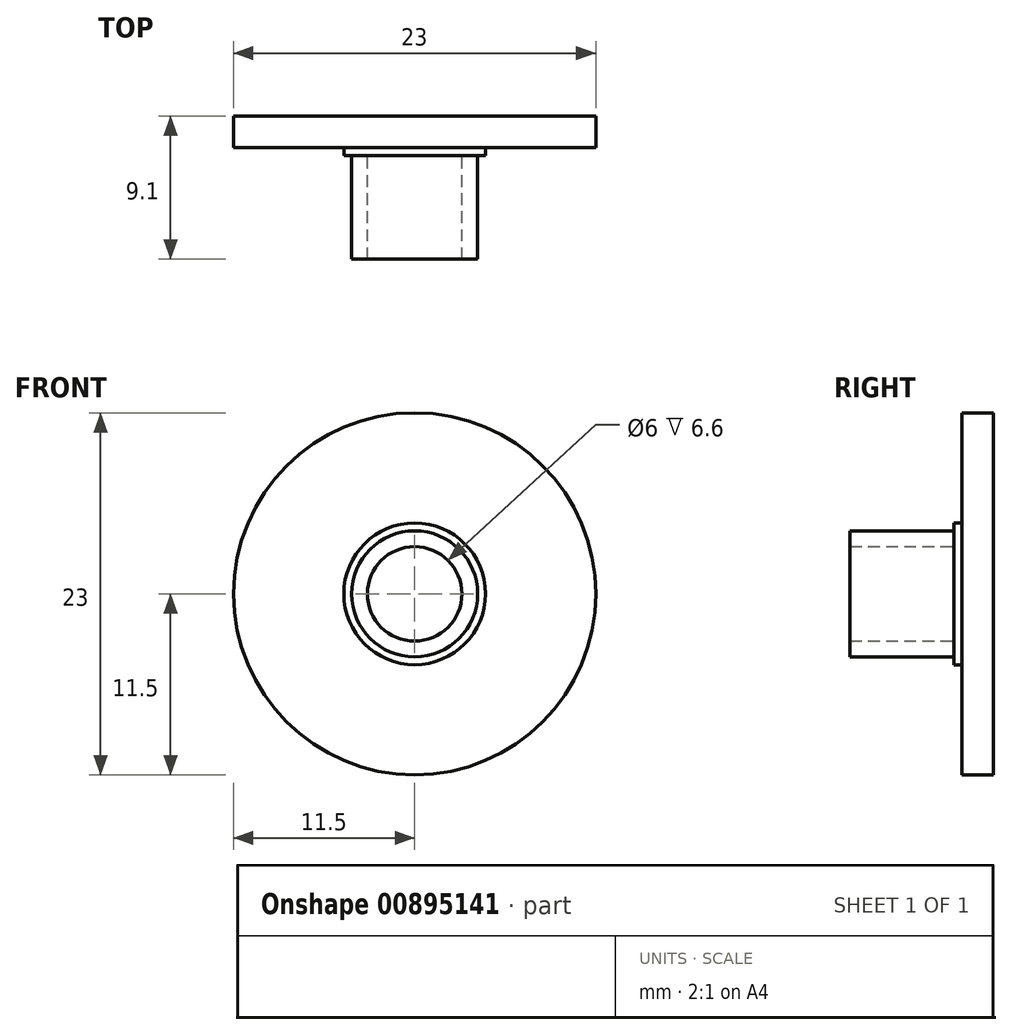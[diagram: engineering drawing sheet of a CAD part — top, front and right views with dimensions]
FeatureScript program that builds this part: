
annotation { "Feature Type Name" : "Feature", "Feature Type Description" : "" }
export const myFeature = defineFeature(function(context is Context, id is Id, definition is map)
    precondition{}
    {
        {
            var Q0;
            Q0=qCreatedBy(makeId("Front.planeOp"),FACE);
            var sketch = newSketch(context, id + "F0", { "sketchPlane" : qUnion([Q0])});
            skCircle(sketch, "E0", {"center": v(0, 0) * mm, "radius": 4 * mm});
            skCircle(sketch, "E1", {"center": v(0, 0) * mm, "radius": 3 * mm});
            skSolve(sketch);
        }
        {
            var Q0;
            Q0=qCreatedBy(makeId("Front.planeOp"),FACE);
            var sketch = newSketch(context, id + "F1", { "sketchPlane" : qUnion([Q0])});
            skCircle(sketch, "E2", {"center": v(0, 0) * mm, "radius": 11.5 * mm});
            skSolve(sketch);
        }
        {
            var Q0;
            Q0=makeQuery(id+"F0.imprint","IMPRINT",FACE,{"disambiguationData":[TD([[makeQuery(id+"F0.imprint","IMPRINT",EDGE,{"derivedFrom":sQuery(id+"F0.wireOp",EDGE,"E0")}),1.0]])]});
            extrude(context, id + "F2", {"entities" : qUnion([Q0]), "depth" : 9.1 * mm, "offsetDistance" : 25 * mm});
        }
        {
            var Q0;
            Q0=makeQuery(id+"F1.imprint","IMPRINT",FACE,{"disambiguationData":[TD([[makeQuery(id+"F1.imprint","IMPRINT",EDGE,{"derivedFrom":sQuery(id+"F1.wireOp",EDGE,"E2")}),1.0]])]});
            extrude(context, id + "F3", {"entities" : qUnion([Q0]), "operationType" : NewBodyOperationType.ADD, "depth" : 2 * mm, "offsetDistance" : 25 * mm});
        }
        {
            var Q0;
            Q0=qCreatedBy(makeId("Front.planeOp"),FACE);
            var sketch = newSketch(context, id + "F4", { "sketchPlane" : qUnion([Q0])});
            skCircle(sketch, "E3", {"center": v(0, 0) * mm, "radius": 4.5 * mm});
            skSolve(sketch);
        }
        {
            var Q0;
            Q0 = qSketchRegion(id + "F4", true);
            extrude(context, id + "F5", {"entities" : qUnion([Q0]), "operationType" : NewBodyOperationType.ADD, "depth" : 2.5 * mm, "offsetDistance" : 25 * mm});
        }
    });
